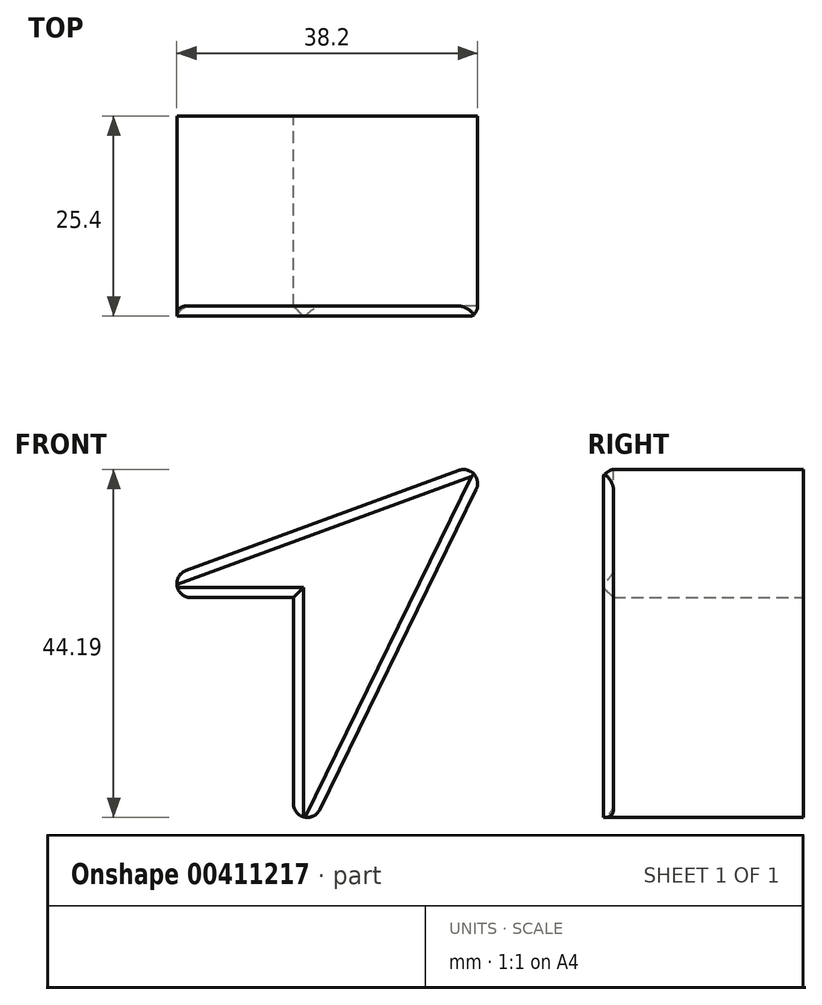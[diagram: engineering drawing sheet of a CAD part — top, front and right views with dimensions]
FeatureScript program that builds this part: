
annotation { "Feature Type Name" : "Feature", "Feature Type Description" : "" }
export const myFeature = defineFeature(function(context is Context, id is Id, definition is map)
    precondition{}
    {
        {
            var Q0;
            Q0=qCreatedBy(makeId("Front.planeOp"),FACE);
            var sketch = newSketch(context, id + "F0", { "sketchPlane" : qUnion([Q0])});
            skLineSegment(sketch, "E0", {"start": v(-48.18, 33.83) * mm, "end": v(-25.16, 33.83) * mm});
            skLineSegment(sketch, "E1", {"start": v(-25.16, 33.83) * mm, "end": v(-25.16, 0) * mm});
            skLineSegment(sketch, "E2", {"start": v(-25.16, 0) * mm, "end": v(0, 51.52) * mm});
            skLineSegment(sketch, "E3", {"start": v(0, 51.52) * mm, "end": v(-48.18, 33.83) * mm});
            skSolve(sketch);
        }
        {
            var Q0;
            Q0=makeQuery(id+"F0.imprint","IMPRINT",FACE,{"disambiguationData":[TD([[makeQuery(id+"F0.imprint","IMPRINT",EDGE,{"derivedFrom":sQuery(id+"F0.wireOp",EDGE,"E0")}),1.0]])]});
            extrude(context, id + "F1", {"entities" : qUnion([Q0]), "depth" : 25.4 * mm});
        }
        {
            var Q0;
            Q0=makeQuery(id+"F1.opExtrude","CAP_EDGE",EDGE,{"disambiguationData":[OSD([sQuery(id+"F0.wireOp",EDGE,"E1")])],"isStart":false});
            var Q1;
            Q1=makeQuery(id+"F1.opExtrude","CAP_EDGE",EDGE,{"disambiguationData":[OSD([sQuery(id+"F0.wireOp",EDGE,"E2")])],"isStart":false});
            var Q2;
            Q2=makeQuery(id+"F1.opExtrude","CAP_EDGE",EDGE,{"disambiguationData":[OSD([sQuery(id+"F0.wireOp",EDGE,"E0")])],"isStart":false});
            var Q3;
            Q3=makeQuery(id+"F1.opExtrude","CAP_EDGE",EDGE,{"disambiguationData":[OSD([sQuery(id+"F0.wireOp",EDGE,"E3")])],"isStart":false});
            chamfer(context, id + "F2", {"entities" : qUnion([Q0, Q1, Q2, Q3]), "width" : 1.27 * mm, "tangentPropagation" : true});
        }
        {
            var Q0;
            Q0=makeQuery(id+"F1.opExtrude","SWEPT_EDGE",EDGE,{"disambiguationData":[OSD([sQuery(id+"F0.wireOp",EDGE,"E1"),sQuery(id+"F0.wireOp",EDGE,"E2")])]});
            var Q1;
            Q1=makeQuery(id+"F1.opExtrude","SWEPT_EDGE",EDGE,{"disambiguationData":[OSD([sQuery(id+"F0.wireOp",EDGE,"E2"),sQuery(id+"F0.wireOp",EDGE,"E3")])]});
            var Q2;
            Q2=makeQuery(id+"F1.opExtrude","SWEPT_EDGE",EDGE,{"disambiguationData":[OSD([sQuery(id+"F0.wireOp",EDGE,"E0"),sQuery(id+"F0.wireOp",EDGE,"E3")])]});
            fillet(context, id + "F3", {"entities" : qUnion([Q0, Q1, Q2]), "radius" : 1.78 * mm, "tangentPropagation" : true, "allowEdgeOverflow" : false});
        }
    });
